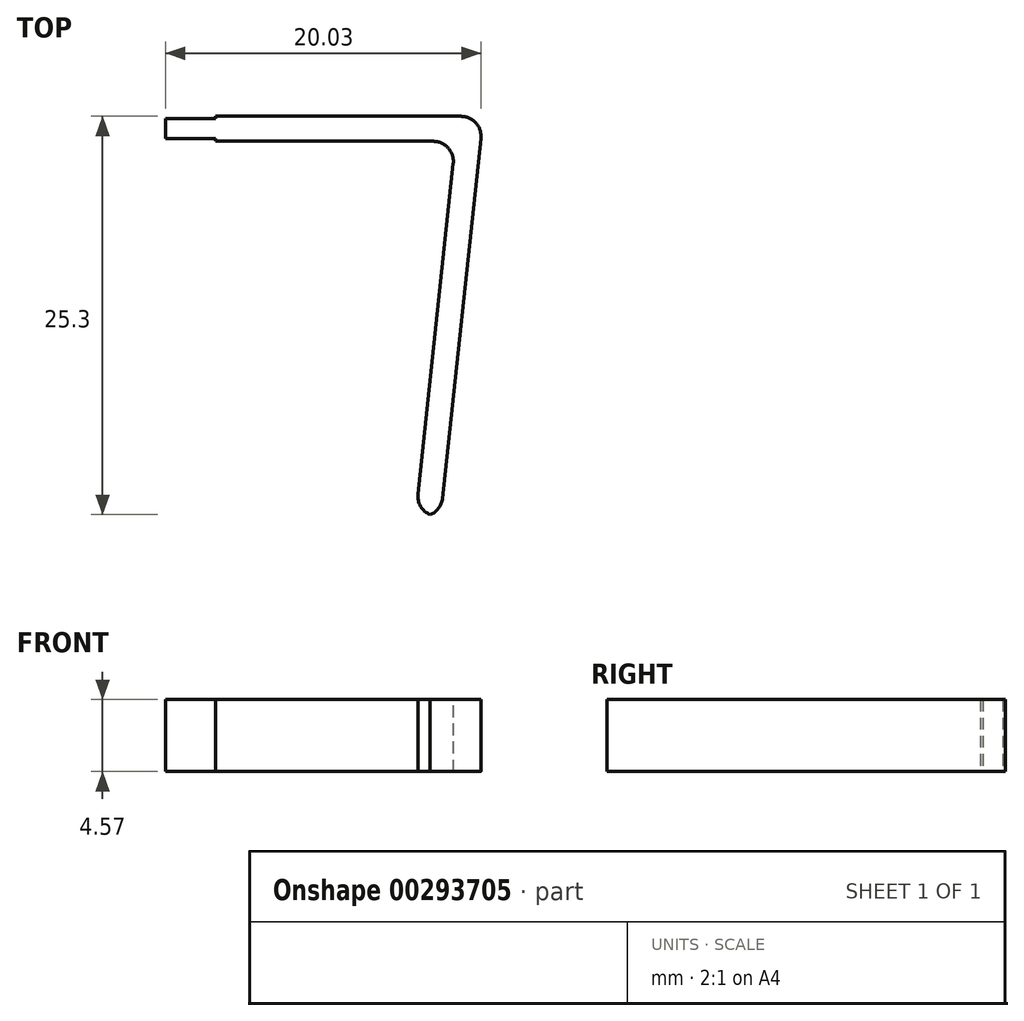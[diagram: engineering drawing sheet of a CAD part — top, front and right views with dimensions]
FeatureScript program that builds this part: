
annotation { "Feature Type Name" : "Feature", "Feature Type Description" : "" }
export const myFeature = defineFeature(function(context is Context, id is Id, definition is map)
    precondition{}
    {
        {
            var Q0;
            Q0=qCreatedBy(makeId("Top.planeOp"),FACE);
            var sketch = newSketch(context, id + "F0", { "sketchPlane" : qUnion([Q0])});
            skLineSegment(sketch, "E0", {"start": v(-20.17, -0.16) * mm, "end": v(-17, -0.16) * mm});
            skLineSegment(sketch, "E1", {"start": v(-17, 0) * mm, "end": v(-17, -0.16) * mm});
            skLineSegment(sketch, "E2", {"start": v(-17, 0) * mm, "end": v(0, 0) * mm});
            skLineSegment(sketch, "E3", {"start": v(0, 0) * mm, "end": v(-2.7, -25.4) * mm});
            skLineSegment(sketch, "E4", {"start": v(-2.7, -25.4) * mm, "end": v(-4.3, -25.4) * mm});
            skLineSegment(sketch, "E5", {"start": v(-4.3, -25.4) * mm, "end": v(-1.76, -1.59) * mm});
            skLineSegment(sketch, "E6", {"start": v(-1.76, -1.59) * mm, "end": v(-17, -1.59) * mm});
            skLineSegment(sketch, "E7", {"start": v(-17, -1.59) * mm, "end": v(-17, -1.43) * mm});
            skLineSegment(sketch, "E8", {"start": v(-17, -1.43) * mm, "end": v(-20.17, -1.43) * mm});
            skLineSegment(sketch, "E9", {"start": v(-20.17, -1.43) * mm, "end": v(-20.17, -0.16) * mm});
            skSolve(sketch);
        }
        {
            var Q0;
            Q0 = qSketchRegion(id + "F0", true);
            extrude(context, id + "F1", {"entities" : qUnion([Q0]), "depth" : 4.57 * mm});
        }
        {
            var Q0;
            Q0=makeQuery(id+"F1.opExtrude","SWEPT_EDGE",EDGE,{"disambiguationData":[OSD([sQuery(id+"F0.wireOp",EDGE,"E4"),sQuery(id+"F0.wireOp",EDGE,"E5")])]});
            var Q1;
            Q1=makeQuery(id+"F1.opExtrude","SWEPT_EDGE",EDGE,{"disambiguationData":[OSD([sQuery(id+"F0.wireOp",EDGE,"E3"),sQuery(id+"F0.wireOp",EDGE,"E4")])]});
            var Q2;
            Q2=makeQuery(id+"F1.opExtrude","SWEPT_EDGE",EDGE,{"disambiguationData":[OSD([sQuery(id+"F0.wireOp",EDGE,"E2"),sQuery(id+"F0.wireOp",EDGE,"E3")])]});
            var Q3;
            Q3=makeQuery(id+"F1.opExtrude","SWEPT_EDGE",EDGE,{"disambiguationData":[OSD([sQuery(id+"F0.wireOp",EDGE,"E5"),sQuery(id+"F0.wireOp",EDGE,"E6")])]});
            fillet(context, id + "F2", {"entities" : qUnion([Q0, Q1, Q2, Q3]), "radius" : 1.27 * mm, "tangentPropagation" : true, "allowEdgeOverflow" : false});
        }
    });
